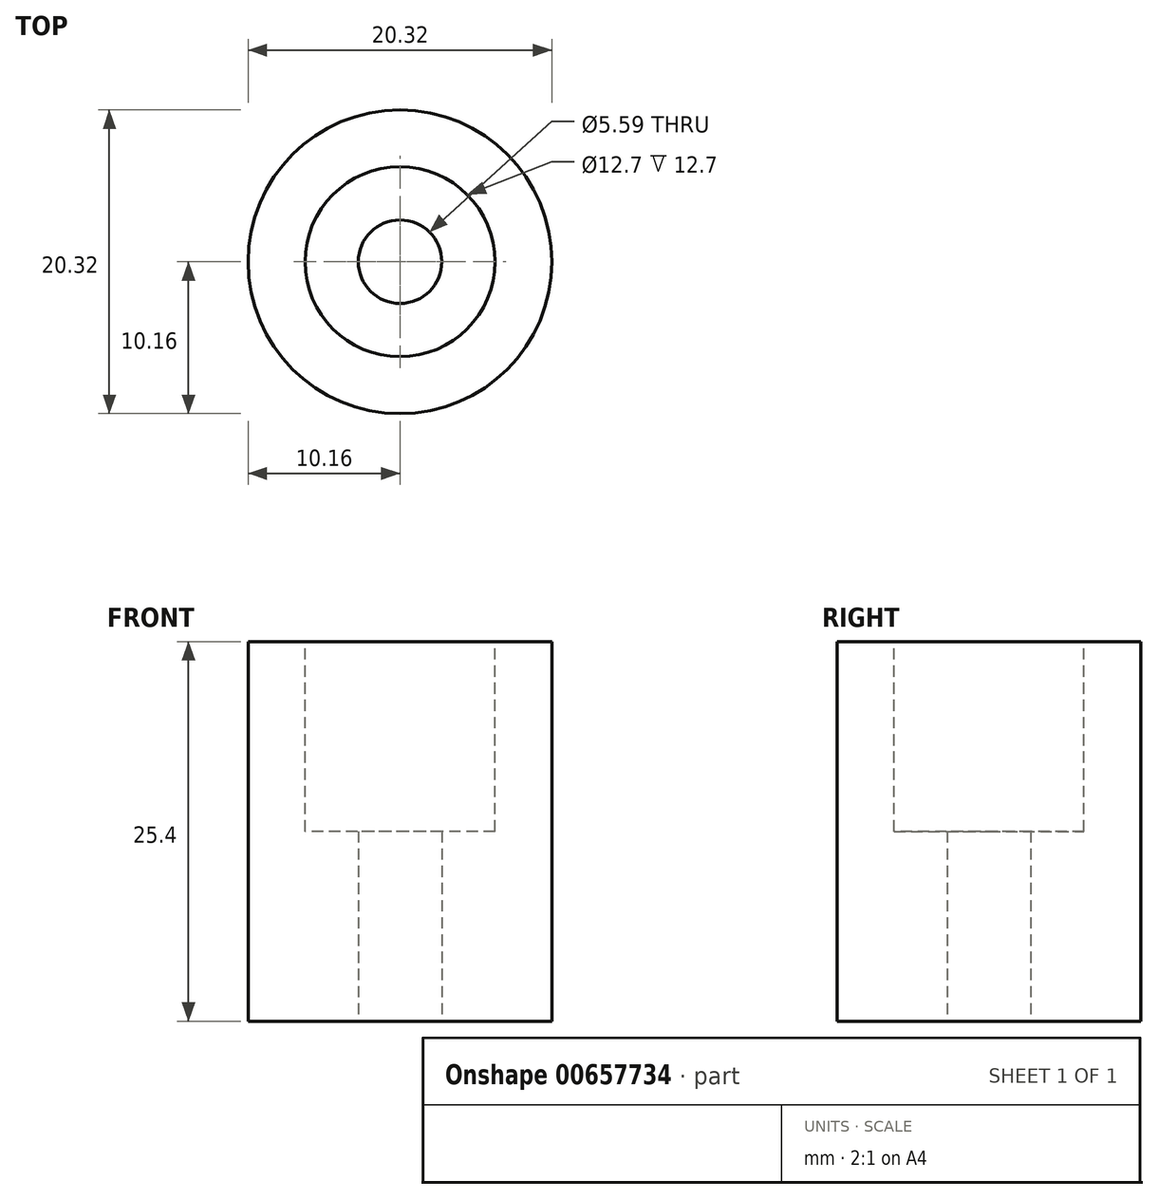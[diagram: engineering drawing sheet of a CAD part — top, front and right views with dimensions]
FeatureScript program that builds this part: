
annotation { "Feature Type Name" : "Feature", "Feature Type Description" : "" }
export const myFeature = defineFeature(function(context is Context, id is Id, definition is map)
    precondition{}
    {
        {
            var Q0;
            Q0=qCreatedBy(makeId("Top.planeOp"),FACE);
            var sketch = newSketch(context, id + "F0", { "sketchPlane" : qUnion([Q0])});
            skCircle(sketch, "E0", {"center": v(0, 0) * mm, "radius": 10.16 * mm});
            skSolve(sketch);
        }
        {
            var Q0;
            Q0=makeQuery(id+"F0.imprint","IMPRINT",FACE,{"disambiguationData":[TD([[makeQuery(id+"F0.imprint","IMPRINT",EDGE,{"derivedFrom":sQuery(id+"F0.wireOp",EDGE,"E0")}),1.0]])]});
            var Q1;
            Q1=sQuery(id+"F0.wireOp",EDGE,"E0");
            extrude(context, id + "F1", {"entities" : qUnion([Q0]), "surfaceEntities" : qUnion([Q1]), "depth" : 25.4 * mm, "offsetDistance" : 25.4 * mm});
        }
        {
            var Q0;
            Q0=makeQuery(id+"F0.imprint","IMPRINT",FACE,{"disambiguationData":[TD([[makeQuery(id+"F0.imprint","IMPRINT",EDGE,{"derivedFrom":sQuery(id+"F0.wireOp",EDGE,"E0")}),1.0]])]});
            var sketch = newSketch(context, id + "F2", { "sketchPlane" : qUnion([Q0])});
            skCircle(sketch, "E1", {"center": v(0, 0) * mm, "radius": 2.8 * mm});
            skSolve(sketch);
        }
        {
            var Q0;
            Q0=makeQuery(id+"F2.imprint","IMPRINT",FACE,{"disambiguationData":[TD([[makeQuery(id+"F2.imprint","IMPRINT",EDGE,{"derivedFrom":sQuery(id+"F2.wireOp",EDGE,"E1")}),1.0]])]});
            var Q1;
            Q1=sQuery(id+"F2.wireOp",EDGE,"E1");
            extrude(context, id + "F3", {"entities" : qUnion([Q0]), "operationType" : NewBodyOperationType.REMOVE, "surfaceEntities" : qUnion([Q1]), "oppositeDirection" : true, "depth" : -76.2 * mm, "offsetDistance" : 25.4 * mm});
        }
        {
            var Q0;
            Q0=makeQuery(id+"F1.opExtrude","CAP_FACE",FACE,{"disambiguationData":[OSD([sQuery(id+"F0.wireOp",EDGE,"E0")])],"isStart":false});
            var sketch = newSketch(context, id + "F4", { "sketchPlane" : qUnion([Q0])});
            skCircle(sketch, "E2", {"center": v(0, 0) * mm, "radius": 6.35 * mm});
            skSolve(sketch);
        }
        {
            var Q0;
            Q0=makeQuery(id+"F4.imprint","IMPRINT",FACE,{"disambiguationData":[TD([[makeQuery(id+"F4.imprint","IMPRINT",EDGE,{"derivedFrom":sQuery(id+"F4.wireOp",EDGE,"E2")}),1.0]])]});
            var Q1;
            Q1=sQuery(id+"F4.wireOp",EDGE,"E2");
            extrude(context, id + "F5", {"entities" : qUnion([Q0]), "operationType" : NewBodyOperationType.REMOVE, "surfaceEntities" : qUnion([Q1]), "oppositeDirection" : true, "depth" : 12.7 * mm, "offsetDistance" : 25.4 * mm});
        }
    });
